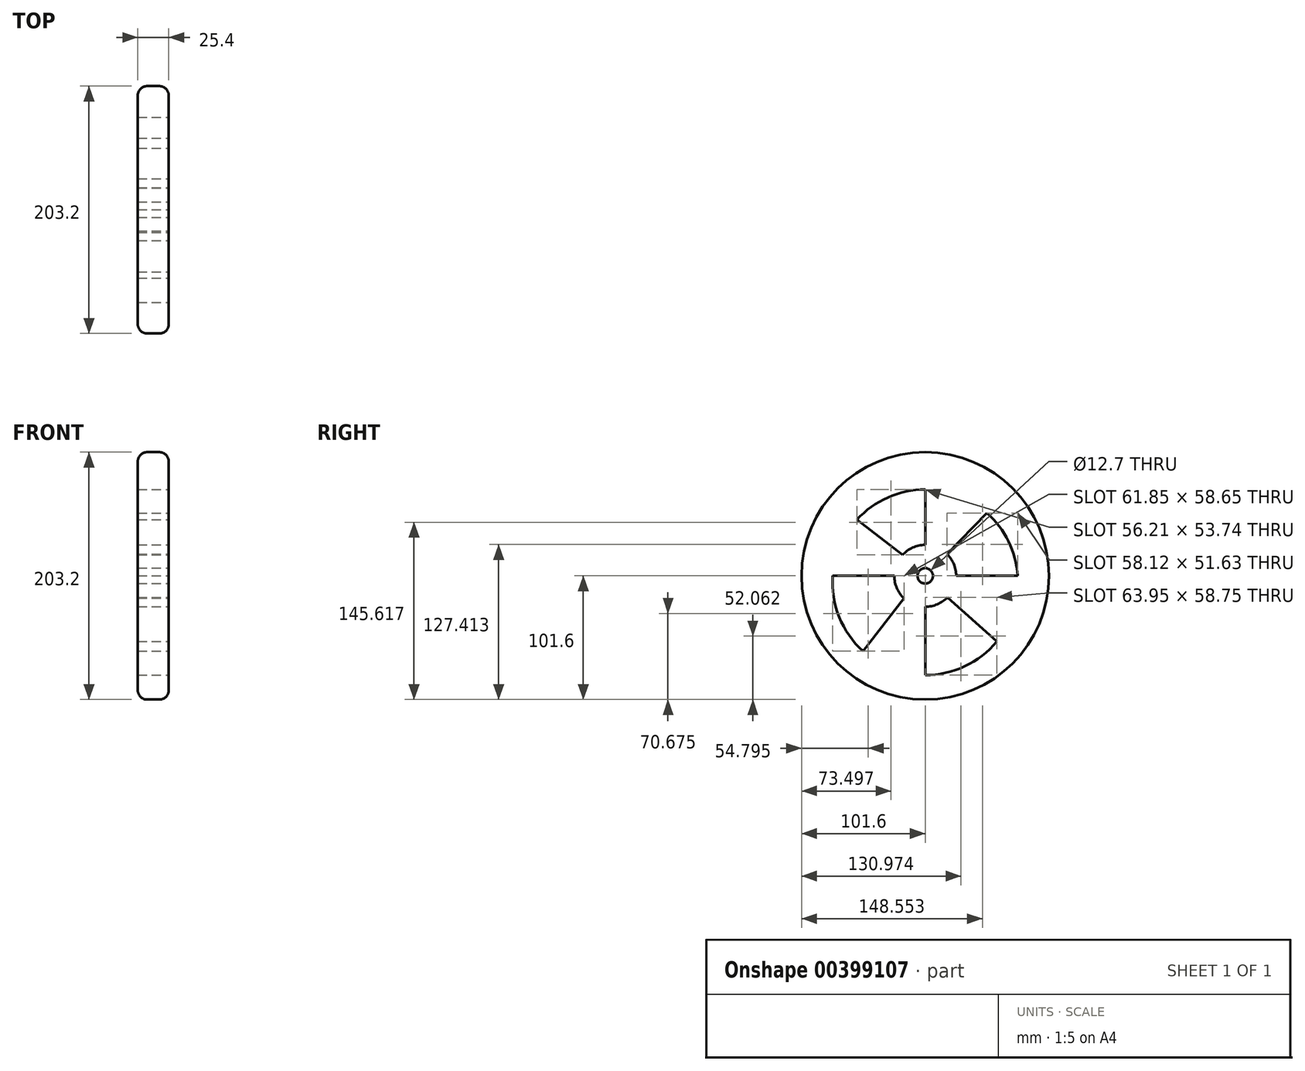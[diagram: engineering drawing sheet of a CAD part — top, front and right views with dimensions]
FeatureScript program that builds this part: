
annotation { "Feature Type Name" : "Feature", "Feature Type Description" : "" }
export const myFeature = defineFeature(function(context is Context, id is Id, definition is map)
    precondition{}
    {
        {
            var Q0;
            Q0=qCreatedBy(makeId("Right.planeOp"),FACE);
            var sketch = newSketch(context, id + "F0", { "sketchPlane" : qUnion([Q0])});
            skCircle(sketch, "E0", {"center": v(0, 0) * mm, "radius": 101.6 * mm});
            skSolve(sketch);
        }
        {
            var Q0;
            Q0=makeQuery(id+"F0.imprint","IMPRINT",FACE,{"disambiguationData":[TD([[makeQuery(id+"F0.imprint","IMPRINT",EDGE,{"derivedFrom":sQuery(id+"F0.wireOp",EDGE,"E0")}),1.0]])]});
            extrude(context, id + "F1", {"entities" : qUnion([Q0]), "depth" : 25.4 * mm});
        }
        {
            var Q0;
            Q0=makeQuery(id+"F1.opExtrude","CAP_FACE",FACE,{"disambiguationData":[OSD([sQuery(id+"F0.wireOp",EDGE,"E0")])],"isStart":false});
            var sketch = newSketch(context, id + "F2", { "sketchPlane" : qUnion([Q0])});
            skCircle(sketch, "E1", {"center": v(0, 0) * mm, "radius": 25.4 * mm});
            skCircle(sketch, "E2", {"center": v(0, -5.31) * mm, "radius": 76.2 * mm});
            skLineSegment(sketch, "E3", {"start": v(0, -25.4) * mm, "end": v(0, -81.51) * mm});
            skLineSegment(sketch, "E4", {"start": v(-25.4, 0) * mm, "end": v(-76.01, 0) * mm});
            skLineSegment(sketch, "E5", {"start": v(0, 25.4) * mm, "end": v(0, 70.89) * mm});
            skLineSegment(sketch, "E6", {"start": v(25.4, 0) * mm, "end": v(76.01, 0) * mm});
            skLineSegment(sketch, "E7", {"start": v(18.35, -17.56) * mm, "end": v(58.75, -53.84) * mm});
            skLineSegment(sketch, "E8", {"start": v(-18.74, 17.15) * mm, "end": v(-56.2, 46.14) * mm});
            skLineSegment(sketch, "E9", {"start": v(-17.48, -18.43) * mm, "end": v(-51.09, -61.85) * mm});
            skLineSegment(sketch, "E10", {"start": v(17.9, 18.03) * mm, "end": v(50.64, 51.63) * mm});
            skSolve(sketch);
        }
        {
            var Q0;
            {var subQ0=sQuery(id+"F2.wireOp",EDGE,"E4");Q0=makeQuery(id+"F2.imprint","IMPRINT",FACE,{"disambiguationData":[TD([[makeQuery(id+"F2.imprint","IMPRINT",EDGE,{"derivedFrom":subQ0}),1.0]])]});}
            var Q1;
            {var subQ0=sQuery(id+"F2.wireOp",EDGE,"E3");Q1=makeQuery(id+"F2.imprint","IMPRINT",FACE,{"disambiguationData":[TD([[makeQuery(id+"F2.imprint","IMPRINT",EDGE,{"derivedFrom":subQ0}),1.0]])]});}
            var Q2;
            {var subQ0=sQuery(id+"F2.wireOp",EDGE,"E6");Q2=makeQuery(id+"F2.imprint","IMPRINT",FACE,{"disambiguationData":[TD([[makeQuery(id+"F2.imprint","IMPRINT",EDGE,{"derivedFrom":subQ0}),1.0]])]});}
            var Q3;
            {var subQ0=sQuery(id+"F2.wireOp",EDGE,"E5");Q3=makeQuery(id+"F2.imprint","IMPRINT",FACE,{"disambiguationData":[TD([[makeQuery(id+"F2.imprint","IMPRINT",EDGE,{"derivedFrom":subQ0}),1.0]])]});}
            extrude(context, id + "F3", {"entities" : qUnion([Q0, Q1, Q2, Q3]), "operationType" : NewBodyOperationType.REMOVE, "oppositeDirection" : true, "depth" : 25.4 * mm});
        }
        {
            var Q0;
            Q0=makeQuery(id+"F1.opExtrude","CAP_EDGE",EDGE,{"disambiguationData":[OSD([sQuery(id+"F0.wireOp",EDGE,"E0")])],"isStart":false});
            var Q1;
            Q1=makeQuery(id+"F1.opExtrude","CAP_EDGE",EDGE,{"disambiguationData":[OSD([sQuery(id+"F0.wireOp",EDGE,"E0")])],"isStart":true});
            fillet(context, id + "F4", {"entities" : qUnion([Q0, Q1]), "radius" : 7.62 * mm, "tangentPropagation" : true, "allowEdgeOverflow" : false});
        }
        {
            var Q0;
            Q0=makeQuery(id+"F1.opExtrude","CAP_FACE",FACE,{"disambiguationData":[OSD([sQuery(id+"F0.wireOp",EDGE,"E0")])],"isStart":false});
            var sketch = newSketch(context, id + "F5", { "sketchPlane" : qUnion([Q0])});
            skCircle(sketch, "E11", {"center": v(0, 0) * mm, "radius": 6.35 * mm});
            skSolve(sketch);
        }
        {
            var Q0;
            Q0=makeQuery(id+"F5.imprint","IMPRINT",FACE,{"disambiguationData":[TD([[makeQuery(id+"F5.imprint","IMPRINT",EDGE,{"derivedFrom":sQuery(id+"F5.wireOp",EDGE,"E11")}),1.0]])]});
            extrude(context, id + "F6", {"entities" : qUnion([Q0]), "operationType" : NewBodyOperationType.REMOVE, "oppositeDirection" : true, "depth" : 25.4 * mm});
        }
    });
